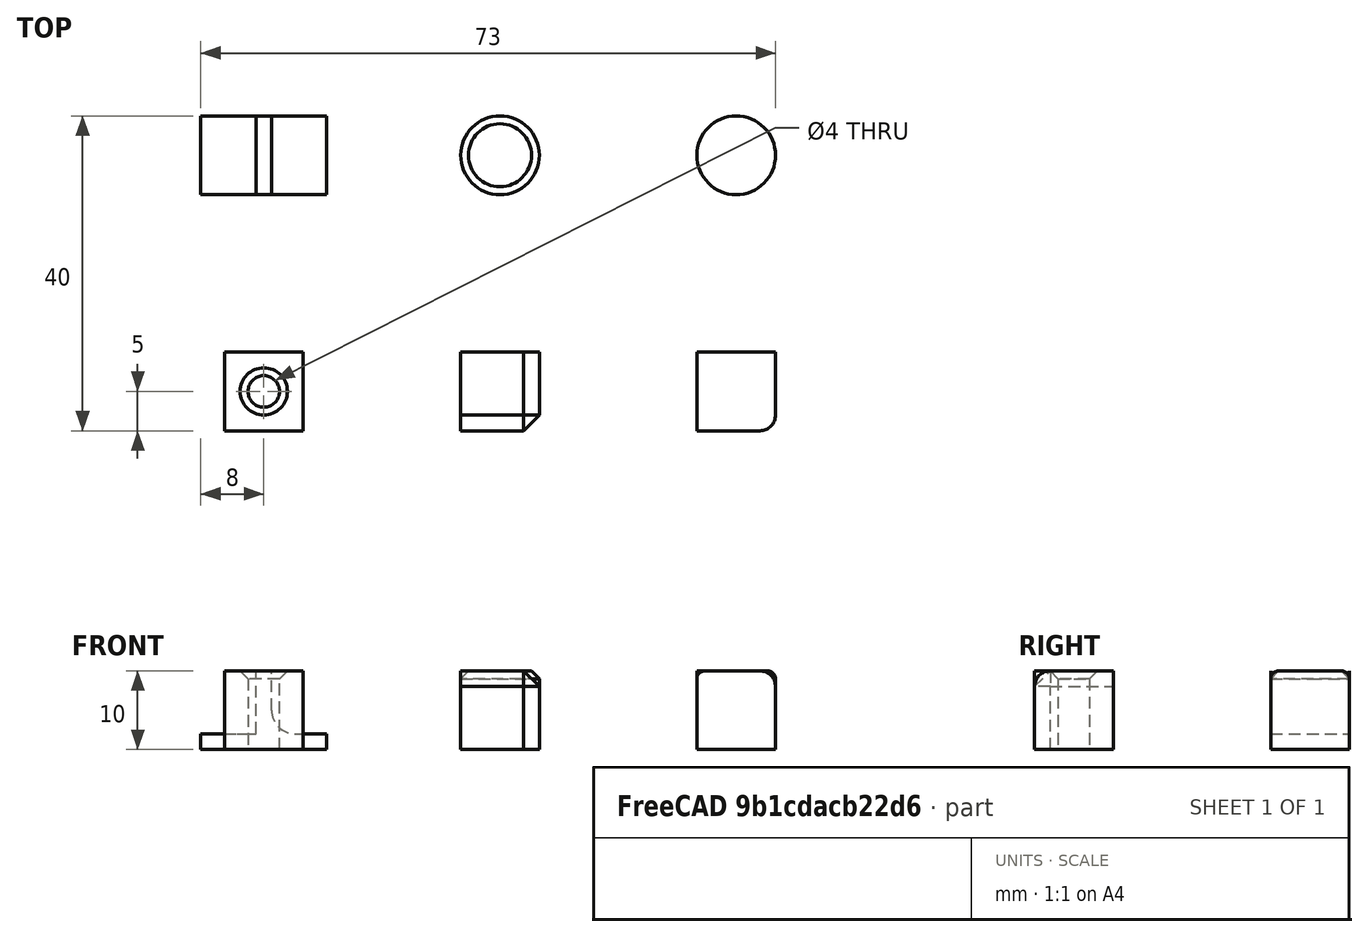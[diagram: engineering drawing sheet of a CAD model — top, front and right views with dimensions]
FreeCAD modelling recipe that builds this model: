
FCSTD DOCUMENT  (FreeCAD 0.21R33694 (Git))
Label: OJT1_T12P01_
License: All rights reserved
LicenseURL: http://en.wikipedia.org/wiki/All_rights_reserved
objects: Part::Box×5, Part::Cylinder×3, Part::Fillet×3, Part::Chamfer×3, Part::Cut×1, Part::MultiFuse×1
note: 16 computed .brp shape members not serialized (recipe doc carries the construction recipe); baked Part::Feature solids carry a one-line shape summary decoded from their .brp

FEATURE [Part::Box] Box  label="Cube"
  AttacherType = Attacher::AttachEngine3D
  Height = 10
  Length = 10
  Width = 10
FEATURE [Part::Box] Box001  label="Cube001"
  AttacherType = Attacher::AttachEngine3D
  Height = 10
  Length = 10
  Placement = pos=(30,0,0) rot=(0,0,1;0rad)
  Width = 10
FEATURE [Part::Box] Box002  label="Cube002"
  AttacherType = Attacher::AttachEngine3D
  Height = 10
  Length = 10
  Placement = pos=(60,0,0) rot=(0,0,1;0rad)
  Width = 10
FEATURE [Part::Cylinder] Cylinder
  Angle = 360
  AttacherType = Attacher::AttachEngine3D
  FirstAngle = 0
  Height = 10
  Placement = pos=(5,5,0) rot=(0,0,1;0rad)
  Radius = 2
  SecondAngle = 0
FEATURE [Part::Cut] Cut
  Base = -> Box
  Refine = true
  Tool = -> Cylinder
FEATURE [Part::Cylinder] Cylinder001
  Angle = 360
  AttacherType = Attacher::AttachEngine3D
  FirstAngle = 0
  Height = 10
  Placement = pos=(65,35,0) rot=(0,0,1;0rad)
  Radius = 5
  SecondAngle = 0
FEATURE [Part::Cylinder] Cylinder002
  Angle = 360
  AttacherType = Attacher::AttachEngine3D
  FirstAngle = 0
  Height = 10
  Placement = pos=(35,35,0) rot=(0,0,1;0rad)
  Radius = 5
  SecondAngle = 0
FEATURE [Part::Box] Box003  label="Cube003"
  AttacherType = Attacher::AttachEngine3D
  Height = 2
  Length = 16
  Placement = pos=(-3,30,0) rot=(0,0,1;0rad)
  Width = 10
FEATURE [Part::Box] Box004  label="Cube004"
  AttacherType = Attacher::AttachEngine3D
  Height = 10
  Length = 2
  Placement = pos=(4,30,0) rot=(0,0,1;0rad)
  Width = 10
FEATURE [Part::MultiFuse] Fusion
  Refine = true
  Shapes = -> [Box003,Box004]
FEATURE [Part::Fillet] Fillet
  Base = -> Box002
  Edges = 3 edges r=2: [Edge5,Edge6,Edge10]
FEATURE [Part::Chamfer] Chamfer
  Base = -> Box001
  Edges = 3 edges r=2: [Edge5,Edge6,Edge10]
FEATURE [Part::Chamfer] Chamfer001
  Base = -> Cut
  Edges = 1 edges r=1: [Edge10]
FEATURE [Part::Fillet] Fillet001
  Base = -> Cylinder001
  Edges = 1 edges r=1: [Edge3]
FEATURE [Part::Chamfer] Chamfer002
  Base = -> Cylinder002
  Edges = 1 edges r=1: [Edge3]
FEATURE [Part::Fillet] Fillet002
  Base = -> Fusion
  Edges = 1 edges r=3: [Edge16]
